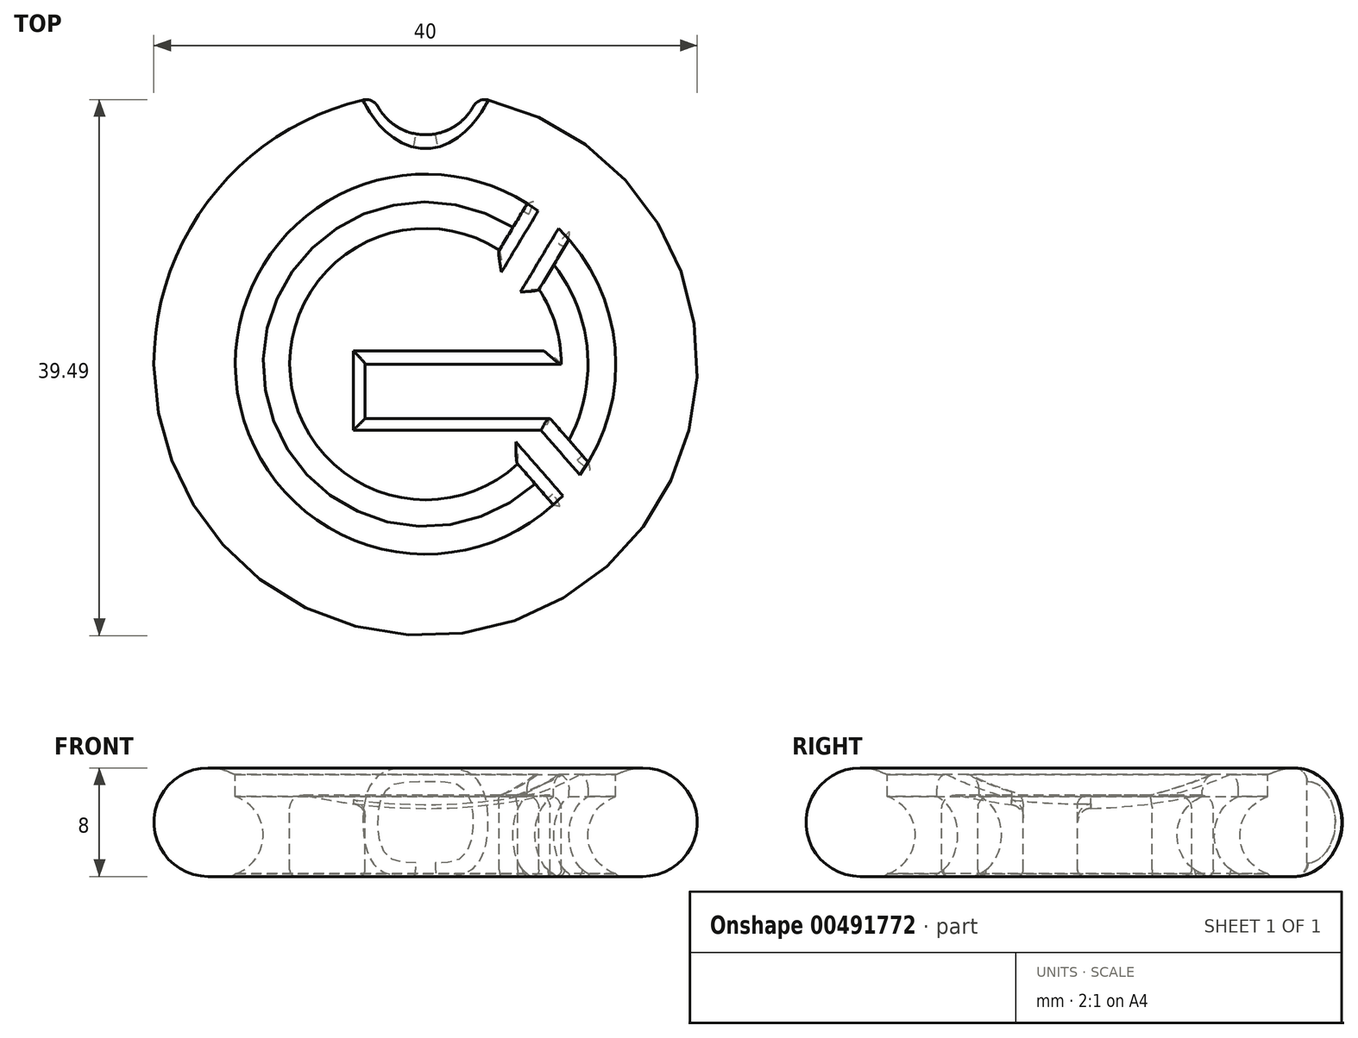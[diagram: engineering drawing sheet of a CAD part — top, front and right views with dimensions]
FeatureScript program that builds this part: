
annotation { "Feature Type Name" : "Feature", "Feature Type Description" : "" }
export const myFeature = defineFeature(function(context is Context, id is Id, definition is map)
    precondition{}
    {
        {
            var Q0;
            Q0=qCreatedBy(makeId("Front.planeOp"),FACE);
            var sketch = newSketch(context, id + "F0", { "sketchPlane" : qUnion([Q0])});
            skArc(sketch, "E0", {"start": v(-14.55, 7.73) * mm, "mid": v(-19.93, 4.74) * mm, "end": v(-16, 0) * mm});
            skArc(sketch, "E1", {"start": v(-14.55, 7.73) * mm, "mid": v(-7.4, 5.69) * mm, "end": v(0, 5) * mm});
            skLineSegment(sketch, "E2", {"start": v(0, 0) * mm, "end": v(-16, 0) * mm});
            skLineSegment(sketch, "E3", {"start": v(0, 0) * mm, "end": v(0, 5) * mm});
            skSolve(sketch);
        }
        {
            var Q0;
            Q0=makeQuery(id+"F0.imprint","IMPRINT",FACE,{"disambiguationData":[TD([[makeQuery(id+"F0.imprint","IMPRINT",EDGE,{"derivedFrom":sQuery(id+"F0.wireOp",EDGE,"E0")}),1.0]])]});
            var Q1;
            Q1=sQuery(id+"F0.wireOp",EDGE,"E3");
            revolve(context, id + "F1", {"entities" : qUnion([Q0]), "axis" : qUnion([Q1]), "revolveType" : RevolveType.FULL});
        }
        {
            var Q0;
            Q0=qCreatedBy(makeId("Top.planeOp"),FACE);
            cPlane(context, id + "F2", {"entities" : qUnion([Q0]), "cplaneType" : CPlaneType.OFFSET, "offset" : 25 * mm, "width" : 150 * mm, "height" : 150 * mm});
        }
        {
            var Q0;
            Q0=qCreatedBy(id+"F2.planeOp",FACE);
            var sketch = newSketch(context, id + "F3", { "sketchPlane" : qUnion([Q0])});
            skArc(sketch, "E4", {"start": v(10, 0) * mm, "mid": v(9.58, 2.87) * mm, "end": v(8.35, 5.5) * mm});
            skLineSegment(sketch, "E5", {"start": v(-4.44, -4) * mm, "end": v(-4.44, 0) * mm});
            skArc(sketch, "E6", {"start": v(11.98, -7.24) * mm, "mid": v(13.95, 1.2) * mm, "end": v(10.57, 9.19) * mm});
            skLineSegment(sketch, "E7", {"start": v(-4.44, -4) * mm, "end": v(9.17, -4) * mm});
            skLineSegment(sketch, "E8", {"start": v(-4.44, 0) * mm, "end": v(10, 0) * mm});
            skLineSegment(sketch, "E9", {"start": v(9.17, -4) * mm, "end": v(11.98, -7.24) * mm});
            skLineSegment(sketch, "E10", {"start": v(6.78, -7.35) * mm, "end": v(9.4, -10.37) * mm});
            skLineSegment(sketch, "E11", {"start": v(8.35, 5.5) * mm, "end": v(10.57, 9.19) * mm});
            skLineSegment(sketch, "E12", {"start": v(5.43, 8.4) * mm, "end": v(7.49, 11.83) * mm});
            skArc(sketch, "E13.trimOffspring", {"start": v(5.43, 8.4) * mm, "mid": v(-9.96, -0.85) * mm, "end": v(6.78, -7.35) * mm});
            skArc(sketch, "E14.trimOffspring", {"start": v(7.49, 11.83) * mm, "mid": v(-13.95, -1.2) * mm, "end": v(9.4, -10.37) * mm});
            skSolve(sketch);
        }
        {
            var Q0;
            Q0=makeQuery(id+"F3.imprint","IMPRINT",FACE,{"disambiguationData":[TD([[makeQuery(id+"F3.imprint","IMPRINT",EDGE,{"derivedFrom":sQuery(id+"F3.wireOp",EDGE,"E10")}),-1.0]])]});
            var Q1;
            Q1=makeQuery(id+"F3.imprint","IMPRINT",FACE,{"disambiguationData":[TD([[makeQuery(id+"F3.imprint","IMPRINT",EDGE,{"derivedFrom":sQuery(id+"F3.wireOp",EDGE,"E4")}),-1.0]])]});
            extrude(context, id + "F4", {"entities" : qUnion([Q0, Q1]), "operationType" : NewBodyOperationType.REMOVE, "oppositeDirection" : true, "depth" : 36 * mm});
        }
        {
            var Q0;
            Q0=qCreatedBy(makeId("Front.planeOp"),FACE);
            var sketch = newSketch(context, id + "F5", { "sketchPlane" : qUnion([Q0])});
            skCircle(sketch, "E15", {"center": v(-14.95, 3.05) * mm, "radius": 3 * mm});
            skSolve(sketch);
        }
        {
            var Q0;
            Q0 = qSketchRegion(id + "F5", true);
            var Q1;
            Q1=sQuery(id+"F0.wireOp",EDGE,"E3");
            revolve(context, id + "F6", {"operationType" : NewBodyOperationType.ADD, "entities" : qUnion([Q0]), "axis" : qUnion([Q1]), "revolveType" : RevolveType.FULL});
        }
        {
            var Q0;
            Q0=qCreatedBy(id+"F2.planeOp",FACE);
            var sketch = newSketch(context, id + "F7", { "sketchPlane" : qUnion([Q0])});
            skCircle(sketch, "E16", {"center": v(0, 20.9) * mm, "radius": 4 * mm});
            skSolve(sketch);
        }
        {
            var Q0;
            Q0 = qSketchRegion(id + "F5", true);
            var Q1;
            Q1=sQuery(id+"F0.wireOp",EDGE,"E3");
            revolve(context, id + "F8", {"operationType" : NewBodyOperationType.ADD, "entities" : qUnion([Q0]), "axis" : qUnion([Q1]), "revolveType" : RevolveType.FULL});
        }
        {
            var Q0;
            Q0=makeQuery(id+"F7.imprint","IMPRINT",FACE,{"disambiguationData":[TD([[makeQuery(id+"F7.imprint","IMPRINT",EDGE,{"derivedFrom":sQuery(id+"F7.wireOp",EDGE,"E16")}),1.0]])]});
            extrude(context, id + "F9", {"entities" : qUnion([Q0]), "operationType" : NewBodyOperationType.REMOVE, "oppositeDirection" : true, "depth" : 31.5 * mm});
        }
        {
            var Q0;
            Q0=makeQuery(id+"F9.boolean.opBoolean","INTERSECT",EDGE,{"derivedFrom":[makeQuery(id+"F1.opRevolve","SWEPT_FACE",FACE,{"disambiguationData":[OSD([sQuery(id+"F0.wireOp",EDGE,"E0")])]}),makeQuery(id+"F9.opExtrude","SWEPT_FACE",FACE,{"disambiguationData":[OSD([sQuery(id+"F7.wireOp",EDGE,"E16")])]})]});
            fillet(context, id + "F10", {"entities" : qUnion([Q0]), "radius" : 1 * mm, "tangentPropagation" : true, "allowEdgeOverflow" : false});
        }
        {
            var Q0;
            Q0=makeQuery(id+"F4.boolean.opBoolean","INTERSECT",EDGE,{"derivedFrom":[makeQuery(id+"F1.opRevolve","SWEPT_FACE",FACE,{"disambiguationData":[OSD([sQuery(id+"F0.wireOp",EDGE,"E1")])]}),makeQuery(id+"F4.opExtrude","SWEPT_FACE",FACE,{"disambiguationData":[OSD([sQuery(id+"F3.wireOp",EDGE,"E13.trimOffspring")])]})]});
            var Q1;
            Q1=makeQuery(id+"F4.boolean.opBoolean","INTERSECT",EDGE,{"derivedFrom":[makeQuery(id+"F1.opRevolve","SWEPT_FACE",FACE,{"disambiguationData":[OSD([sQuery(id+"F0.wireOp",EDGE,"E1")])]}),makeQuery(id+"F4.opExtrude","SWEPT_FACE",FACE,{"disambiguationData":[OSD([sQuery(id+"F3.wireOp",EDGE,"E12")])]})]});
            var Q2;
            Q2=makeQuery(id+"F4.boolean.opBoolean","INTERSECT",EDGE,{"derivedFrom":[makeQuery(id+"F1.opRevolve","SWEPT_FACE",FACE,{"disambiguationData":[OSD([sQuery(id+"F0.wireOp",EDGE,"E1")])]}),makeQuery(id+"F4.opExtrude","SWEPT_FACE",FACE,{"disambiguationData":[OSD([sQuery(id+"F3.wireOp",EDGE,"E11")])]})]});
            var Q3;
            Q3=makeQuery(id+"F4.boolean.opBoolean","INTERSECT",EDGE,{"derivedFrom":[makeQuery(id+"F1.opRevolve","SWEPT_FACE",FACE,{"disambiguationData":[OSD([sQuery(id+"F0.wireOp",EDGE,"E1")])]}),makeQuery(id+"F4.opExtrude","SWEPT_FACE",FACE,{"disambiguationData":[OSD([sQuery(id+"F3.wireOp",EDGE,"E4")])]})]});
            var Q4;
            Q4=makeQuery(id+"F4.boolean.opBoolean","INTERSECT",EDGE,{"derivedFrom":[makeQuery(id+"F1.opRevolve","SWEPT_FACE",FACE,{"disambiguationData":[OSD([sQuery(id+"F0.wireOp",EDGE,"E1")])]}),makeQuery(id+"F4.opExtrude","SWEPT_FACE",FACE,{"disambiguationData":[OSD([sQuery(id+"F3.wireOp",EDGE,"E7")])]})]});
            var Q5;
            Q5=makeQuery(id+"F4.boolean.opBoolean","INTERSECT",EDGE,{"derivedFrom":[makeQuery(id+"F1.opRevolve","SWEPT_FACE",FACE,{"disambiguationData":[OSD([sQuery(id+"F0.wireOp",EDGE,"E1")])]}),makeQuery(id+"F4.opExtrude","SWEPT_FACE",FACE,{"disambiguationData":[OSD([sQuery(id+"F3.wireOp",EDGE,"E5")])]})]});
            var Q6;
            Q6=makeQuery(id+"F4.boolean.opBoolean","INTERSECT",EDGE,{"derivedFrom":[makeQuery(id+"F1.opRevolve","SWEPT_FACE",FACE,{"disambiguationData":[OSD([sQuery(id+"F0.wireOp",EDGE,"E1")])]}),makeQuery(id+"F4.opExtrude","SWEPT_FACE",FACE,{"disambiguationData":[OSD([sQuery(id+"F3.wireOp",EDGE,"E10")])]})]});
            var Q7;
            Q7=makeQuery(id+"F4.boolean.opBoolean","INTERSECT",EDGE,{"derivedFrom":[makeQuery(id+"F1.opRevolve","SWEPT_FACE",FACE,{"disambiguationData":[OSD([sQuery(id+"F0.wireOp",EDGE,"E1")])]}),makeQuery(id+"F4.opExtrude","SWEPT_FACE",FACE,{"disambiguationData":[OSD([sQuery(id+"F3.wireOp",EDGE,"E8")])]})]});
            var Q8;
            Q8=makeQuery(id+"F4.boolean.opBoolean","INTERSECT",EDGE,{"derivedFrom":[makeQuery(id+"F1.opRevolve","SWEPT_FACE",FACE,{"disambiguationData":[OSD([sQuery(id+"F0.wireOp",EDGE,"E1")])]}),makeQuery(id+"F4.opExtrude","SWEPT_FACE",FACE,{"disambiguationData":[OSD([sQuery(id+"F3.wireOp",EDGE,"E9")])]})]});
            fillet(context, id + "F11", {"entities" : qUnion([Q0, Q1, Q2, Q3, Q4, Q5, Q6, Q7, Q8]), "radius" : 1 * mm, "tangentPropagation" : true, "allowEdgeOverflow" : false});
        }
        {
            var Q0;
            Q0=makeQuery(id+"F4.boolean.opBoolean","INTERSECT",EDGE,{"derivedFrom":[makeQuery(id+"F1.opRevolve","SWEPT_FACE",FACE,{"disambiguationData":[OSD([sQuery(id+"F0.wireOp",EDGE,"E2")])]}),makeQuery(id+"F4.opExtrude","SWEPT_FACE",FACE,{"disambiguationData":[OSD([sQuery(id+"F3.wireOp",EDGE,"E10")])]})]});
            var Q1;
            Q1=makeQuery(id+"F4.boolean.opBoolean","INTERSECT",EDGE,{"derivedFrom":[makeQuery(id+"F1.opRevolve","SWEPT_FACE",FACE,{"disambiguationData":[OSD([sQuery(id+"F0.wireOp",EDGE,"E2")])]}),makeQuery(id+"F4.opExtrude","SWEPT_FACE",FACE,{"disambiguationData":[OSD([sQuery(id+"F3.wireOp",EDGE,"E13.trimOffspring")])]})]});
            var Q2;
            Q2=makeQuery(id+"F4.boolean.opBoolean","INTERSECT",EDGE,{"derivedFrom":[makeQuery(id+"F1.opRevolve","SWEPT_FACE",FACE,{"disambiguationData":[OSD([sQuery(id+"F0.wireOp",EDGE,"E2")])]}),makeQuery(id+"F4.opExtrude","SWEPT_FACE",FACE,{"disambiguationData":[OSD([sQuery(id+"F3.wireOp",EDGE,"E7")])]})]});
            var Q3;
            Q3=makeQuery(id+"F4.boolean.opBoolean","INTERSECT",EDGE,{"derivedFrom":[makeQuery(id+"F1.opRevolve","SWEPT_FACE",FACE,{"disambiguationData":[OSD([sQuery(id+"F0.wireOp",EDGE,"E2")])]}),makeQuery(id+"F4.opExtrude","SWEPT_FACE",FACE,{"disambiguationData":[OSD([sQuery(id+"F3.wireOp",EDGE,"E5")])]})]});
            var Q4;
            Q4=makeQuery(id+"F4.boolean.opBoolean","INTERSECT",EDGE,{"derivedFrom":[makeQuery(id+"F1.opRevolve","SWEPT_FACE",FACE,{"disambiguationData":[OSD([sQuery(id+"F0.wireOp",EDGE,"E2")])]}),makeQuery(id+"F4.opExtrude","SWEPT_FACE",FACE,{"disambiguationData":[OSD([sQuery(id+"F3.wireOp",EDGE,"E8")])]})]});
            var Q5;
            Q5=makeQuery(id+"F4.boolean.opBoolean","INTERSECT",EDGE,{"derivedFrom":[makeQuery(id+"F1.opRevolve","SWEPT_FACE",FACE,{"disambiguationData":[OSD([sQuery(id+"F0.wireOp",EDGE,"E2")])]}),makeQuery(id+"F4.opExtrude","SWEPT_FACE",FACE,{"disambiguationData":[OSD([sQuery(id+"F3.wireOp",EDGE,"E4")])]})]});
            var Q6;
            Q6=makeQuery(id+"F4.boolean.opBoolean","INTERSECT",EDGE,{"derivedFrom":[makeQuery(id+"F1.opRevolve","SWEPT_FACE",FACE,{"disambiguationData":[OSD([sQuery(id+"F0.wireOp",EDGE,"E2")])]}),makeQuery(id+"F4.opExtrude","SWEPT_FACE",FACE,{"disambiguationData":[OSD([sQuery(id+"F3.wireOp",EDGE,"E11")])]})]});
            var Q7;
            Q7=makeQuery(id+"F4.boolean.opBoolean","INTERSECT",EDGE,{"derivedFrom":[makeQuery(id+"F1.opRevolve","SWEPT_FACE",FACE,{"disambiguationData":[OSD([sQuery(id+"F0.wireOp",EDGE,"E2")])]}),makeQuery(id+"F4.opExtrude","SWEPT_FACE",FACE,{"disambiguationData":[OSD([sQuery(id+"F3.wireOp",EDGE,"E9")])]})]});
            var Q8;
            Q8=makeQuery(id+"F4.boolean.opBoolean","INTERSECT",EDGE,{"derivedFrom":[makeQuery(id+"F1.opRevolve","SWEPT_FACE",FACE,{"disambiguationData":[OSD([sQuery(id+"F0.wireOp",EDGE,"E2")])]}),makeQuery(id+"F4.opExtrude","SWEPT_FACE",FACE,{"disambiguationData":[OSD([sQuery(id+"F3.wireOp",EDGE,"E12")])]})]});
            fillet(context, id + "F12", {"entities" : qUnion([Q0, Q1, Q2, Q3, Q4, Q5, Q6, Q7, Q8]), "radius" : .5 * mm, "tangentPropagation" : true, "allowEdgeOverflow" : false});
        }
        {
            var Q0;
            Q0=makeQuery(id+"F4.boolean.opBoolean","INTERSECT",EDGE,{"derivedFrom":[makeQuery(id+"F1.opRevolve","SWEPT_FACE",FACE,{"disambiguationData":[OSD([sQuery(id+"F0.wireOp",EDGE,"E2")])]}),makeQuery(id+"F4.opExtrude","SWEPT_FACE",FACE,{"disambiguationData":[OSD([sQuery(id+"F3.wireOp",EDGE,"E14.trimOffspring")])]})]});
            var Q1;
            Q1=makeQuery(id+"F4.boolean.opBoolean","INTERSECT",EDGE,{"derivedFrom":[makeQuery(id+"F1.opRevolve","SWEPT_FACE",FACE,{"disambiguationData":[OSD([sQuery(id+"F0.wireOp",EDGE,"E2")])]}),makeQuery(id+"F4.opExtrude","SWEPT_FACE",FACE,{"disambiguationData":[OSD([sQuery(id+"F3.wireOp",EDGE,"E6")])]})]});
            fillet(context, id + "F13", {"entities" : qUnion([Q0, Q1]), "radius" : .5 * mm, "tangentPropagation" : true, "allowEdgeOverflow" : false});
        }
    });
